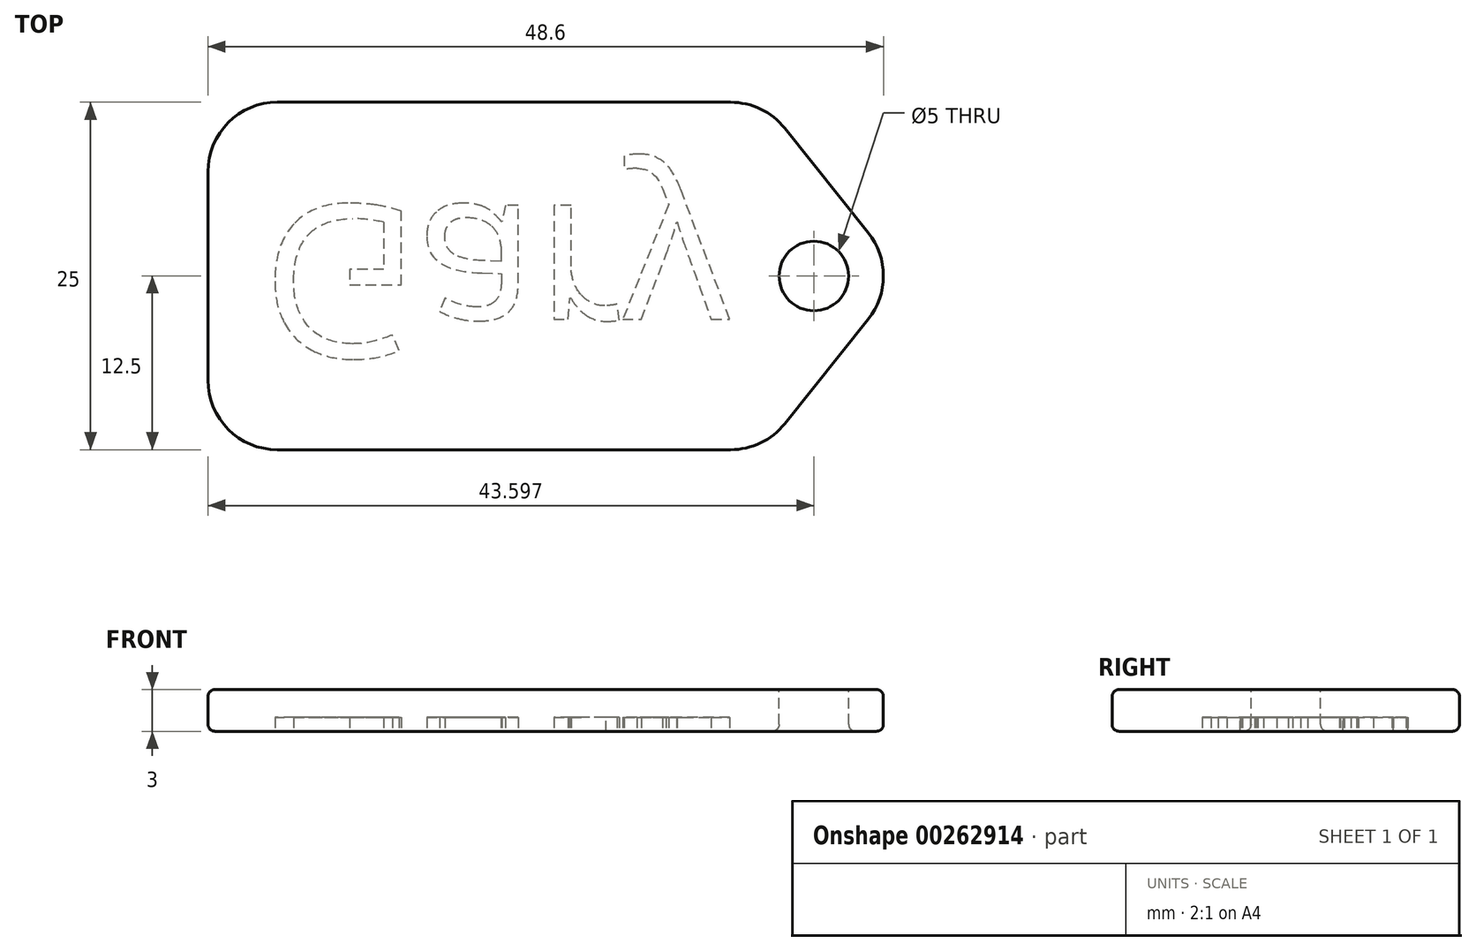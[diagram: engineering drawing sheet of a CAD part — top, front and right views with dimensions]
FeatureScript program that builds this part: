
annotation { "Feature Type Name" : "Feature", "Feature Type Description" : "" }
export const myFeature = defineFeature(function(context is Context, id is Id, definition is map)
    precondition{}
    {
        {
            var Q0;
            Q0=qCreatedBy(makeId("Top.planeOp"),FACE);
            var sketch = newSketch(context, id + "F0", { "sketchPlane" : qUnion([Q0])});
            skLineSegment(sketch, "E0.bottom", {"start": v(-20, 12.5) * mm, "end": v(20, 12.5) * mm});
            skLineSegment(sketch, "E0.top", {"start": v(-20, -12.5) * mm, "end": v(20, -12.5) * mm});
            skLineSegment(sketch, "E0.left", {"start": v(-20, 12.5) * mm, "end": v(-20, -12.5) * mm});
            skPoint(sketch, "E0.middle", {"position": v(0, 0) * mm});
            skPoint(sketch, "E1", {"position": v(30, 0) * mm});
            skLineSegment(sketch, "E2", {"start": v(20, -12.5) * mm, "end": v(30, 0) * mm});
            skLineSegment(sketch, "E3", {"start": v(20, 12.5) * mm, "end": v(30, 0) * mm});
            skSolve(sketch);
        }
        {
            var Q0;
            Q0=makeQuery(id+"F0.imprint","IMPRINT",FACE,{"disambiguationData":[TD([[makeQuery(id+"F0.imprint","IMPRINT",EDGE,{"derivedFrom":sQuery(id+"F0.wireOp",EDGE,"E0.bottom")}),-1.0]])]});
            extrude(context, id + "F1", {"entities" : qUnion([Q0]), "depth" : 3 * mm});
        }
        {
            var Q0;
            Q0=makeQuery(id+"F1.opExtrude","SWEPT_EDGE",EDGE,{"disambiguationData":[OSD([sQuery(id+"F0.wireOp",EDGE,"E2"),sQuery(id+"F0.wireOp",EDGE,"E3")])]});
            fillet(context, id + "F2", {"entities" : qUnion([Q0]), "radius" : 5 * mm, "tangentPropagation" : true, "allowEdgeOverflow" : false});
        }
        {
            var Q0;
            Q0=makeQuery(id+"F1.opExtrude","CAP_FACE",FACE,{"disambiguationData":[OSD([sQuery(id+"F0.wireOp",EDGE,"E0.bottom"),sQuery(id+"F0.wireOp",EDGE,"E0.top"),sQuery(id+"F0.wireOp",EDGE,"E0.left"),sQuery(id+"F0.wireOp",EDGE,"E2"),sQuery(id+"F0.wireOp",EDGE,"E3")])],"isStart":false});
            var sketch = newSketch(context, id + "F3", { "sketchPlane" : qUnion([Q0])});
            skPoint(sketch, "E4", {"position": v(23.6, 0) * mm});
            skSolve(sketch);
        }
        {
            var Q0;
            Q0=sQuery(id+"F3.wireOp",VERTEX,"E4");
            var Q1;
            Q1=makeQuery(id+"F1.opExtrude","SWEPT_BODY",BODY,{"disambiguationData":[OSD([sQuery(id+"F0.wireOp",EDGE,"E0.bottom"),sQuery(id+"F0.wireOp",EDGE,"E0.top"),sQuery(id+"F0.wireOp",EDGE,"E0.left"),sQuery(id+"F0.wireOp",EDGE,"E2"),sQuery(id+"F0.wireOp",EDGE,"E3")])]});
            hole(context, id + "F4", {"style" : HoleStyle.SIMPLE, "endStyle" : HoleEndStyle.THROUGH, "holeDiameter" : 5 * mm, "tappedDepth" : 12 * mm, "tapClearance" : 3, "locations" : qUnion([Q0]), "scope" : qUnion([Q1])});
        }
        {
            var Q0;
            Q0=makeQuery(id+"F1.opExtrude","SWEPT_EDGE",EDGE,{"disambiguationData":[OSD([sQuery(id+"F0.wireOp",EDGE,"E0.bottom"),sQuery(id+"F0.wireOp",EDGE,"E3")])]});
            var Q1;
            Q1=makeQuery(id+"F1.opExtrude","SWEPT_EDGE",EDGE,{"disambiguationData":[OSD([sQuery(id+"F0.wireOp",EDGE,"E0.bottom"),sQuery(id+"F0.wireOp",EDGE,"E0.left")])]});
            var Q2;
            Q2=makeQuery(id+"F1.opExtrude","SWEPT_EDGE",EDGE,{"disambiguationData":[OSD([sQuery(id+"F0.wireOp",EDGE,"E0.top"),sQuery(id+"F0.wireOp",EDGE,"E0.left")])]});
            var Q3;
            Q3=makeQuery(id+"F1.opExtrude","SWEPT_EDGE",EDGE,{"disambiguationData":[OSD([sQuery(id+"F0.wireOp",EDGE,"E0.top"),sQuery(id+"F0.wireOp",EDGE,"E2")])]});
            fillet(context, id + "F5", {"entities" : qUnion([Q0, Q1, Q2, Q3]), "radius" : 5 * mm, "tangentPropagation" : true, "allowEdgeOverflow" : false});
        }
        {
            var Q0;
            Q0=makeQuery(id+"F1.opExtrude","CAP_EDGE",EDGE,{"disambiguationData":[OSD([sQuery(id+"F0.wireOp",EDGE,"E0.bottom")])],"isStart":false});
            var Q1;
            Q1=makeQuery(id+"F4.hole-0.boolean.opBoolean","COPY",EDGE,{"derivedFrom":makeQuery(id+"F4.hole-0.opRevolve","SWEPT_EDGE",EDGE,{"disambiguationData":[OSD([sQuery(id+"F4.hole-0.sketch.wireOp",EDGE,"core_line_2"),sQuery(id+"F4.hole-0.sketch.wireOp",EDGE,"core_line_3")])]})});
            var Q2;
            Q2=makeQuery(id+"F1.opExtrude","CAP_FACE",FACE,{"disambiguationData":[OSD([sQuery(id+"F0.wireOp",EDGE,"E0.bottom"),sQuery(id+"F0.wireOp",EDGE,"E0.top"),sQuery(id+"F0.wireOp",EDGE,"E0.left"),sQuery(id+"F0.wireOp",EDGE,"E2"),sQuery(id+"F0.wireOp",EDGE,"E3")])],"isStart":true});
            fillet(context, id + "F6", {"entities" : qUnion([Q0, Q1, Q2]), "radius" : 0.5 * mm, "tangentPropagation" : true, "allowEdgeOverflow" : false});
        }
        {
            var Q0;
            Q0=makeQuery(id+"F1.opExtrude","CAP_FACE",FACE,{"disambiguationData":[OSD([sQuery(id+"F0.wireOp",EDGE,"E0.bottom"),sQuery(id+"F0.wireOp",EDGE,"E0.top"),sQuery(id+"F0.wireOp",EDGE,"E0.left"),sQuery(id+"F0.wireOp",EDGE,"E2"),sQuery(id+"F0.wireOp",EDGE,"E3")])],"isStart":true});
            var sketch = newSketch(context, id + "F7", { "sketchPlane" : qUnion([Q0])});
            skText(sketch, "E5", { "text": "Gary", "fontName": "OpenSans-Regular.ttf"});
            const initialGuessF7  = {"E5": [-0.01612, -0.00509, 1, 0, 0.01104]};
            skSetInitialGuess(sketch, initialGuessF7);
            skSolve(sketch);
        }
        {
            var Q0;
            Q0 = qSketchRegion(id + "F7", true);
            extrude(context, id + "F8", {"entities" : qUnion([Q0]), "operationType" : NewBodyOperationType.REMOVE, "oppositeDirection" : true, "depth" : 1 * mm});
        }
    });
